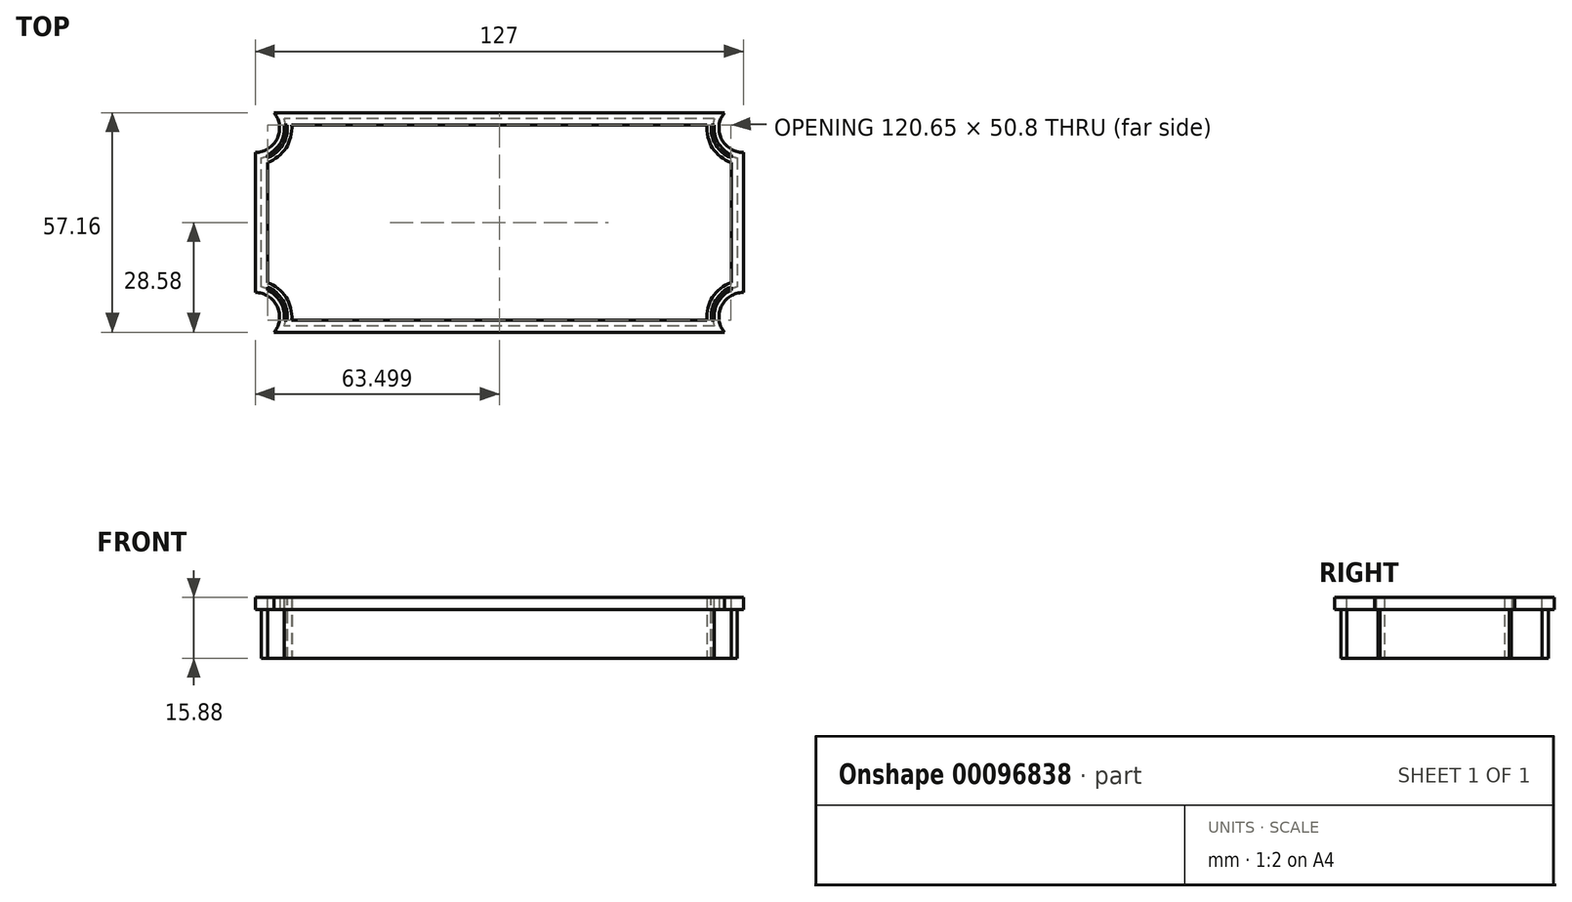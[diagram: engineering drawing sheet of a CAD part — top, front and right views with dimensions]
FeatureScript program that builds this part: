
annotation { "Feature Type Name" : "Feature", "Feature Type Description" : "" }
export const myFeature = defineFeature(function(context is Context, id is Id, definition is map)
    precondition{}
    {
        {
            var Q0;
            Q0=qCreatedBy(makeId("Top.planeOp"),FACE);
            var sketch = newSketch(context, id + "F0", { "sketchPlane" : qUnion([Q0])});
            skLineSegment(sketch, "E0.top", {"start": v(58.57, -28.57) * mm, "end": v(-58.57, -28.58) * mm});
            skPoint(sketch, "E0.middle", {"position": v(0, 0) * mm});
            skArc(sketch, "E1.MirrorC", {"start": v(-63.5, -18.23) * mm, "mid": v(-57.77, -21.85) * mm, "end": v(-58.57, -28.58) * mm});
            skArc(sketch, "E2.MirrorC", {"start": v(63.5, -18.23) * mm, "mid": v(57.77, -21.85) * mm, "end": v(58.57, -28.57) * mm});
            skArc(sketch, "E3.2", {"start": v(-60.33, -15.6) * mm, "mid": v(-55.5, -19.42) * mm, "end": v(-54.01, -25.4) * mm});
            skLineSegment(sketch, "E3.4", {"start": v(54.01, -25.4) * mm, "end": v(-54.01, -25.4) * mm});
            skArc(sketch, "E3.5", {"start": v(60.33, -15.6) * mm, "mid": v(55.5, -19.42) * mm, "end": v(54.01, -25.4) * mm});
            skArc(sketch, "E4.MirrorCS", {"start": v(-60.33, 15.6) * mm, "mid": v(-55.5, 19.42) * mm, "end": v(-54.01, 25.4) * mm});
            skLineSegment(sketch, "E5.MirrorCS", {"start": v(58.57, 28.57) * mm, "end": v(-58.57, 28.58) * mm});
            skArc(sketch, "E6.MirrorCS", {"start": v(-63.5, 18.23) * mm, "mid": v(-57.77, 21.85) * mm, "end": v(-58.57, 28.58) * mm});
            skArc(sketch, "E7.MirrorCS", {"start": v(60.33, 15.6) * mm, "mid": v(55.5, 19.42) * mm, "end": v(54.01, 25.4) * mm});
            skLineSegment(sketch, "E8.MirrorCS", {"start": v(54.01, 25.4) * mm, "end": v(-54.01, 25.4) * mm});
            skArc(sketch, "E9.MirrorCS", {"start": v(63.5, 18.23) * mm, "mid": v(57.77, 21.85) * mm, "end": v(58.57, 28.57) * mm});
            skLineSegment(sketch, "E10", {"start": v(-63.5, 18.23) * mm, "end": v(-63.5, -18.23) * mm});
            skLineSegment(sketch, "E11", {"start": v(-60.33, -15.6) * mm, "end": v(-60.33, 15.6) * mm});
            skLineSegment(sketch, "E12", {"start": v(60.33, 15.6) * mm, "end": v(60.33, -15.6) * mm});
            skLineSegment(sketch, "E13", {"start": v(63.5, -18.23) * mm, "end": v(63.5, 18.23) * mm});
            skSolve(sketch);
        }
        {
            var Q0;
            Q0=makeQuery(id+"F0.imprint","IMPRINT",FACE,{"disambiguationData":[TD([[makeQuery(id+"F0.imprint","IMPRINT",EDGE,{"derivedFrom":sQuery(id+"F0.wireOp",EDGE,"E0.top")}),-1.0]])]});
            extrude(context, id + "F1", {"entities" : qUnion([Q0]), "depth" : 3.17 * mm});
        }
        {
            var Q0;
            Q0=makeQuery(id+"F1.opExtrude","CAP_FACE",FACE,{"disambiguationData":[OSD([sQuery(id+"F0.wireOp",EDGE,"E0.bottom"),sQuery(id+"F0.wireOp",EDGE,"E0.top"),sQuery(id+"F0.wireOp",EDGE,"E0.left"),sQuery(id+"F0.wireOp",EDGE,"E0.right"),sQuery(id+"F0.wireOp",EDGE,"w1uiDken-AQbg-yEvY-p1R7-PD8J70mOPkLS"),sQuery(id+"F0.wireOp",EDGE,"6af09c78-26ff-43e5-9641-da19c5421ef50.MirrorC"),sQuery(id+"F0.wireOp",EDGE,"E1.MirrorC"),sQuery(id+"F0.wireOp",EDGE,"E2.MirrorC"),sQuery(id+"F0.wireOp",EDGE,"E3.0"),sQuery(id+"F0.wireOp",EDGE,"E3.1"),sQuery(id+"F0.wireOp",EDGE,"E3.2"),sQuery(id+"F0.wireOp",EDGE,"E3.3"),sQuery(id+"F0.wireOp",EDGE,"E3.4"),sQuery(id+"F0.wireOp",EDGE,"E3.5"),sQuery(id+"F0.wireOp",EDGE,"E3.6"),sQuery(id+"F0.wireOp",EDGE,"E3.7")])],"isStart":true});
            var sketch = newSketch(context, id + "F2", { "sketchPlane" : qUnion([Q0])});
            skLineSegment(sketch, "E14.0", {"start": v(54.01, 25.4) * mm, "end": v(-54.01, 25.4) * mm});
            skArc(sketch, "E14.1", {"start": v(60.33, 15.6) * mm, "mid": v(55.5, 19.42) * mm, "end": v(54.01, 25.4) * mm});
            skLineSegment(sketch, "E14.2", {"start": v(60.33, -15.6) * mm, "end": v(60.33, 15.6) * mm});
            skArc(sketch, "E14.3", {"start": v(60.33, -15.6) * mm, "mid": v(55.5, -19.42) * mm, "end": v(54.01, -25.4) * mm});
            skLineSegment(sketch, "E14.4", {"start": v(54.01, -25.4) * mm, "end": v(-54.01, -25.4) * mm});
            skArc(sketch, "E14.5", {"start": v(-60.33, -15.6) * mm, "mid": v(-55.5, -19.42) * mm, "end": v(-54.01, -25.4) * mm});
            skLineSegment(sketch, "E14.6", {"start": v(-60.33, 15.6) * mm, "end": v(-60.33, -15.6) * mm});
            skArc(sketch, "E14.7", {"start": v(-60.33, 15.6) * mm, "mid": v(-55.5, 19.42) * mm, "end": v(-54.01, 25.4) * mm});
            skLineSegment(sketch, "E15.0", {"start": v(61.93, -16.81) * mm, "end": v(61.93, 16.81) * mm});
            skArc(sketch, "E15.1", {"start": v(61.93, 16.81) * mm, "mid": v(56.66, 20.57) * mm, "end": v(55.96, 27) * mm});
            skArc(sketch, "E15.2", {"start": v(61.93, -16.81) * mm, "mid": v(56.66, -20.57) * mm, "end": v(55.96, -27) * mm});
            skLineSegment(sketch, "E15.3", {"start": v(55.96, 27) * mm, "end": v(-55.96, 27) * mm});
            skLineSegment(sketch, "E15.4", {"start": v(55.96, -27) * mm, "end": v(-55.96, -27) * mm});
            skArc(sketch, "E15.5", {"start": v(-61.93, -16.81) * mm, "mid": v(-56.67, -20.57) * mm, "end": v(-55.96, -27) * mm});
            skLineSegment(sketch, "E15.6", {"start": v(-61.93, 16.81) * mm, "end": v(-61.93, -16.81) * mm});
            skArc(sketch, "E15.7", {"start": v(-61.93, 16.81) * mm, "mid": v(-56.67, 20.57) * mm, "end": v(-55.96, 27) * mm});
            skSolve(sketch);
        }
        {
            var Q0;
            Q0 = qSketchRegion(id + "F2", true);
            extrude(context, id + "F3", {"entities" : qUnion([Q0]), "operationType" : NewBodyOperationType.ADD, "depth" : 12.7 * mm});
        }
        {
            var Q0;
            Q0=makeQuery(id+"F1.opExtrude","CAP_FACE",FACE,{"disambiguationData":[OSD([sQuery(id+"F0.wireOp",EDGE,"E0.bottom"),sQuery(id+"F0.wireOp",EDGE,"E0.top"),sQuery(id+"F0.wireOp",EDGE,"E0.left"),sQuery(id+"F0.wireOp",EDGE,"E0.right"),sQuery(id+"F0.wireOp",EDGE,"w1uiDken-AQbg-yEvY-p1R7-PD8J70mOPkLS"),sQuery(id+"F0.wireOp",EDGE,"6af09c78-26ff-43e5-9641-da19c5421ef50.MirrorC"),sQuery(id+"F0.wireOp",EDGE,"E1.MirrorC"),sQuery(id+"F0.wireOp",EDGE,"E2.MirrorC"),sQuery(id+"F0.wireOp",EDGE,"E3.0"),sQuery(id+"F0.wireOp",EDGE,"E3.1"),sQuery(id+"F0.wireOp",EDGE,"E3.2"),sQuery(id+"F0.wireOp",EDGE,"E3.3"),sQuery(id+"F0.wireOp",EDGE,"E3.4"),sQuery(id+"F0.wireOp",EDGE,"E3.5"),sQuery(id+"F0.wireOp",EDGE,"E3.6"),sQuery(id+"F0.wireOp",EDGE,"E3.7")])],"isStart":false});
            var sketch = newSketch(context, id + "F4", { "sketchPlane" : qUnion([Q0])});
            skArc(sketch, "E16.0", {"start": v(-60.33, 17.65) * mm, "mid": v(-56.88, 20.82) * mm, "end": v(-55.93, 25.4) * mm});
            skArc(sketch, "E17.0", {"start": v(-60.33, 16.82) * mm, "mid": v(-56.32, 20.26) * mm, "end": v(-55.16, 25.4) * mm});
            skLineSegment(sketch, "E18", {"start": v(-55.16, 25.4) * mm, "end": v(-55.93, 25.4) * mm});
            skLineSegment(sketch, "E19", {"start": v(-60.33, 16.82) * mm, "end": v(-60.33, 17.65) * mm});
            skLineSegment(sketch, "E20.MirrorCS", {"start": v(60.33, 16.82) * mm, "end": v(60.33, 17.65) * mm});
            skLineSegment(sketch, "E21.MirrorCS", {"start": v(55.16, 25.4) * mm, "end": v(55.93, 25.4) * mm});
            skArc(sketch, "E22.MirrorCS", {"start": v(60.33, 16.82) * mm, "mid": v(56.32, 20.26) * mm, "end": v(55.16, 25.4) * mm});
            skArc(sketch, "E23.MirrorCS", {"start": v(60.33, 17.65) * mm, "mid": v(56.88, 20.82) * mm, "end": v(55.93, 25.4) * mm});
            skLineSegment(sketch, "E24.MirrorCS", {"start": v(-60.33, -16.82) * mm, "end": v(-60.33, -17.65) * mm});
            skLineSegment(sketch, "E25.MirrorCS", {"start": v(-55.16, -25.4) * mm, "end": v(-55.93, -25.4) * mm});
            skLineSegment(sketch, "E26.MirrorCS", {"start": v(60.33, -16.82) * mm, "end": v(60.33, -17.65) * mm});
            skLineSegment(sketch, "E27.MirrorCS", {"start": v(55.16, -25.4) * mm, "end": v(55.93, -25.4) * mm});
            skArc(sketch, "E28.MirrorCS", {"start": v(-60.33, -17.65) * mm, "mid": v(-56.88, -20.82) * mm, "end": v(-55.93, -25.4) * mm});
            skArc(sketch, "E29.MirrorCS", {"start": v(-60.33, -16.82) * mm, "mid": v(-56.32, -20.26) * mm, "end": v(-55.16, -25.4) * mm});
            skArc(sketch, "E30.MirrorCS", {"start": v(60.33, -17.65) * mm, "mid": v(56.88, -20.82) * mm, "end": v(55.93, -25.4) * mm});
            skArc(sketch, "E31.MirrorCS", {"start": v(60.33, -16.82) * mm, "mid": v(56.32, -20.26) * mm, "end": v(55.16, -25.4) * mm});
            skSolve(sketch);
        }
        {
            var Q0;
            Q0 = qSketchRegion(id + "F4", true);
            extrude(context, id + "F5", {"entities" : qUnion([Q0]), "operationType" : NewBodyOperationType.REMOVE, "oppositeDirection" : true, "depth" : 25.4 * mm});
        }
    });
